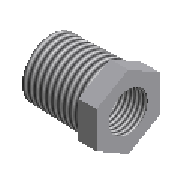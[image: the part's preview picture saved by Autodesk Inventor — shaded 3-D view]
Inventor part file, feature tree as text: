
AUTODESK INVENTOR PART (.ipt)
format: ipt  version: 2015 (Build 190159000, 159)  size: 203,264 bytes
history: native  units: mm (DEFAULTED — no unit token found)
features: other x8, sketch x2, revolve x1, extrude x1
ambient origin geometry x8: Origin, YZ Plane, XZ Plane, XY Plane, X Axis, Y Axis, Z Axis, Center Point
bodies: Body1 (feature_tree)
feature tree (12):
  revolve  "Revolve1"  [1 undecoded]
  extrude  "Extrude1"  Depth=5.0mm
  other  "Work Axis2"
  other  "Work Point3"
  other  "Work Axis3"
  other  "Work Point4"
  other  "Work Axis4"
  other  "Work Axis5"
  other  "Work Point5"
  other  "Work Point6"
  sketch  "Sketch1"  dims[d0=11.445mm d1=17.0mm]
  sketch  "Sketch2"  dims[d8=90.0deg d2=5.0mm d3=0.0mm d11=25.4mm d12=0.0mm d13=25.4mm d14=0.0mm d4=17.5mm d5=5.0mm d7=0.312398mm d9=12.4mm d10=5.833333mm d38=6.35mm d39=16.662mm]
note: 1 required parameter value undecoded (feature->parameter linkage not recoverable at this tier; creation-order binding heuristic only, values carry confidence <= 0.55)
